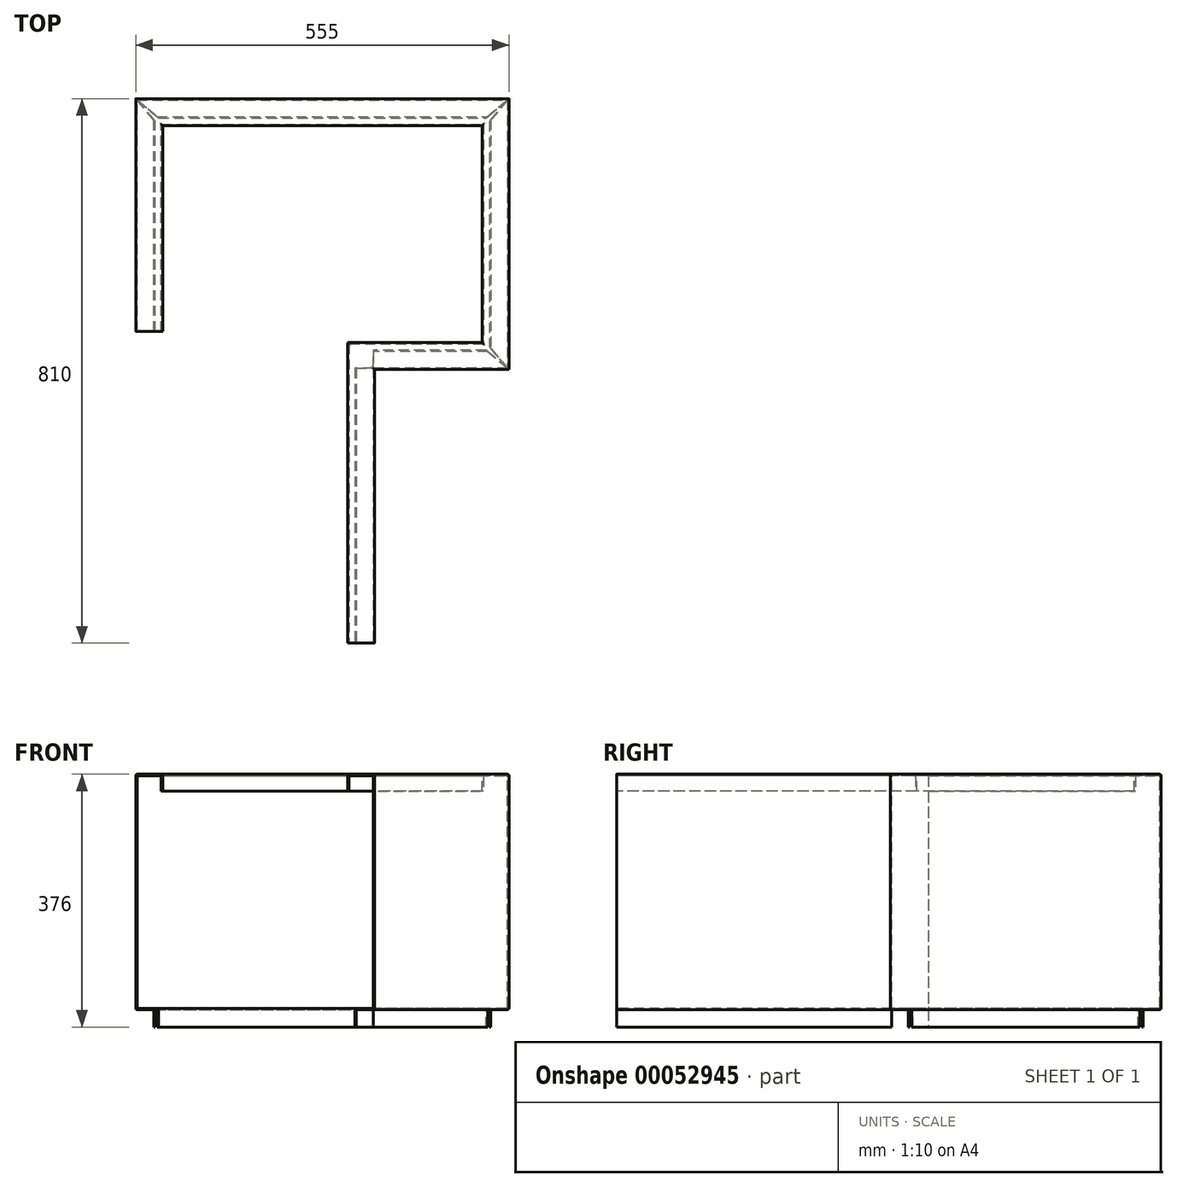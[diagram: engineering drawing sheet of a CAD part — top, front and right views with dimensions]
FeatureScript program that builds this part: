
annotation { "Feature Type Name" : "Feature", "Feature Type Description" : "" }
export const myFeature = defineFeature(function(context is Context, id is Id, definition is map)
    precondition{}
    {
        {
            var Q0;
            Q0=qCreatedBy(makeId("Front.planeOp"),FACE);
            var sketch = newSketch(context, id + "F0", { "sketchPlane" : qUnion([Q0])});
            skLineSegment(sketch, "E0", {"start": v(2, 0) * mm, "end": v(38, 0) * mm});
            skLineSegment(sketch, "E1", {"start": v(40, -2) * mm, "end": v(40, -25) * mm});
            skLineSegment(sketch, "E2", {"start": v(0, -2) * mm, "end": v(0, -348) * mm});
            skLineSegment(sketch, "E3", {"start": v(2, -350) * mm, "end": v(25, -350) * mm});
            skLineSegment(sketch, "E4", {"start": v(27, -352) * mm, "end": v(27, -376) * mm});
            skLineSegment(sketch, "E5.0", {"start": v(29, -350) * mm, "end": v(29, -376) * mm});
            skLineSegment(sketch, "E5.1", {"start": v(38, -4) * mm, "end": v(38, -25) * mm});
            skLineSegment(sketch, "E5.2", {"start": v(4, -2) * mm, "end": v(36, -2) * mm});
            skLineSegment(sketch, "E5.3", {"start": v(2, -4) * mm, "end": v(2, -346) * mm});
            skLineSegment(sketch, "E5.4", {"start": v(4, -348) * mm, "end": v(27, -348) * mm});
            skLineSegment(sketch, "E6", {"start": v(29, -376) * mm, "end": v(27, -376) * mm});
            skLineSegment(sketch, "E7", {"start": v(38, -25) * mm, "end": v(40, -25) * mm});
            skPoint(sketch, "E8.visualSharp", {"position": v(40, 0) * mm});
            skArc(sketch, "E8.filletArc", {"start": v(40, -2) * mm, "mid": v(39.41, -0.59) * mm, "end": v(38, 0) * mm});
            skArc(sketch, "E9.filletArc", {"start": v(38, -4) * mm, "mid": v(37.41, -2.59) * mm, "end": v(36, -2) * mm});
            skPoint(sketch, "E10.visualSharp", {"position": v(2, -2) * mm});
            skArc(sketch, "E10.filletArc", {"start": v(4, -2) * mm, "mid": v(2.59, -2.59) * mm, "end": v(2, -4) * mm});
            skPoint(sketch, "E11.visualSharp", {"position": v(0, 0) * mm});
            skArc(sketch, "E11.filletArc", {"start": v(2, 0) * mm, "mid": v(0.59, -0.59) * mm, "end": v(0, -2) * mm});
            skPoint(sketch, "E12.visualSharp", {"position": v(2, -348) * mm});
            skArc(sketch, "E12.filletArc", {"start": v(2, -346) * mm, "mid": v(2.59, -347.41) * mm, "end": v(4, -348) * mm});
            skPoint(sketch, "E13.visualSharp", {"position": v(0, -350) * mm});
            skArc(sketch, "E13.filletArc", {"start": v(0, -348) * mm, "mid": v(0.59, -349.41) * mm, "end": v(2, -350) * mm});
            skPoint(sketch, "E14.visualSharp", {"position": v(27, -350) * mm});
            skArc(sketch, "E14.filletArc", {"start": v(27, -352) * mm, "mid": v(26.41, -350.59) * mm, "end": v(25, -350) * mm});
            skPoint(sketch, "E15.visualSharp", {"position": v(29, -348) * mm});
            skArc(sketch, "E15.filletArc", {"start": v(29, -350) * mm, "mid": v(28.41, -348.59) * mm, "end": v(27, -348) * mm});
            skSolve(sketch);
        }
        {
            var Q0;
            Q0=qCreatedBy(makeId("Top.planeOp"),FACE);
            var sketch = newSketch(context, id + "F1", { "sketchPlane" : qUnion([Q0])});
            skLineSegment(sketch, "E16", {"start": v(0, 0) * mm, "end": v(0, 346) * mm});
            skLineSegment(sketch, "E17", {"start": v(0, 346) * mm, "end": v(555, 346) * mm});
            skLineSegment(sketch, "E18", {"start": v(555, 346) * mm, "end": v(555, -57) * mm});
            skLineSegment(sketch, "E19", {"start": v(555, -57) * mm, "end": v(355, -57) * mm});
            skLineSegment(sketch, "E20", {"start": v(355, -57) * mm, "end": v(355, -464) * mm});
            skSolve(sketch);
        }
        {
            var Q0;
            Q0=makeQuery(id+"F0.imprint","IMPRINT",FACE,{"disambiguationData":[TD([[makeQuery(id+"F0.imprint","IMPRINT",EDGE,{"derivedFrom":sQuery(id+"F0.wireOp",EDGE,"E0")}),-1.0]])]});
            var Q1;
            Q1=sQuery(id+"F1.wireOp",EDGE,"E16");
            var Q2;
            Q2=sQuery(id+"F1.wireOp",EDGE,"E17");
            var Q3;
            Q3=sQuery(id+"F1.wireOp",EDGE,"E18");
            var Q4;
            Q4=sQuery(id+"F1.wireOp",EDGE,"E19");
            var Q5;
            Q5=sQuery(id+"F1.wireOp",EDGE,"E20");
            sweep(context, id + "F2", {"profiles" : qUnion([Q0]), "path" : qUnion([Q1, Q2, Q3, Q4, Q5])});
        }
        {
            var Q0;
            Q0=makeQuery(id+"F2.opSweep","SWEPT_FACE",FACE,{"disambiguationData":[OSD([sQuery(id+"F0.wireOp",EDGE,"E5.4"),sQuery(id+"F1.wireOp",EDGE,"E16")])]});
            var sketch = newSketch(context, id + "F3", { "sketchPlane" : qUnion([Q0])});
            skLineSegment(sketch, "E21", {"start": v(29, 311.82) * mm, "end": v(2, 344) * mm});
            skLineSegment(sketch, "E22", {"start": v(2, 344) * mm, "end": v(34.18, 317) * mm});
            skLineSegment(sketch, "E23", {"start": v(34.18, 317) * mm, "end": v(29, 317) * mm});
            skLineSegment(sketch, "E24", {"start": v(29, 317) * mm, "end": v(29, 311.82) * mm});
            skLineSegment(sketch, "E25", {"start": v(553, 344) * mm, "end": v(520.82, 317) * mm});
            skLineSegment(sketch, "E26", {"start": v(520.82, 317) * mm, "end": v(526, 317) * mm});
            skLineSegment(sketch, "E27", {"start": v(526, 317) * mm, "end": v(526, 311.82) * mm});
            skLineSegment(sketch, "E28", {"start": v(526, 311.82) * mm, "end": v(553, 344) * mm});
            skLineSegment(sketch, "E29", {"start": v(553, -55) * mm, "end": v(526, -22.82) * mm});
            skLineSegment(sketch, "E30", {"start": v(526, -22.82) * mm, "end": v(526, -28) * mm});
            skLineSegment(sketch, "E31", {"start": v(526, -28) * mm, "end": v(520.82, -28) * mm});
            skLineSegment(sketch, "E32", {"start": v(520.82, -28) * mm, "end": v(553, -55) * mm});
            skLineSegment(sketch, "E33", {"start": v(353, -55) * mm, "end": v(353, -28) * mm});
            skLineSegment(sketch, "E34", {"start": v(353, -28) * mm, "end": v(326, -28) * mm});
            skLineSegment(sketch, "E35", {"start": v(326, -28) * mm, "end": v(326, -55) * mm});
            skLineSegment(sketch, "E36", {"start": v(326, -55) * mm, "end": v(353, -55) * mm});
            skSolve(sketch);
        }
        {
            var Q0;
            Q0 = qSketchRegion(id + "F3", true);
            extrude(context, id + "F4", {"entities" : qUnion([Q0]), "operationType" : NewBodyOperationType.REMOVE, "oppositeDirection" : true, "depth" : 40 * mm});
        }
    });
